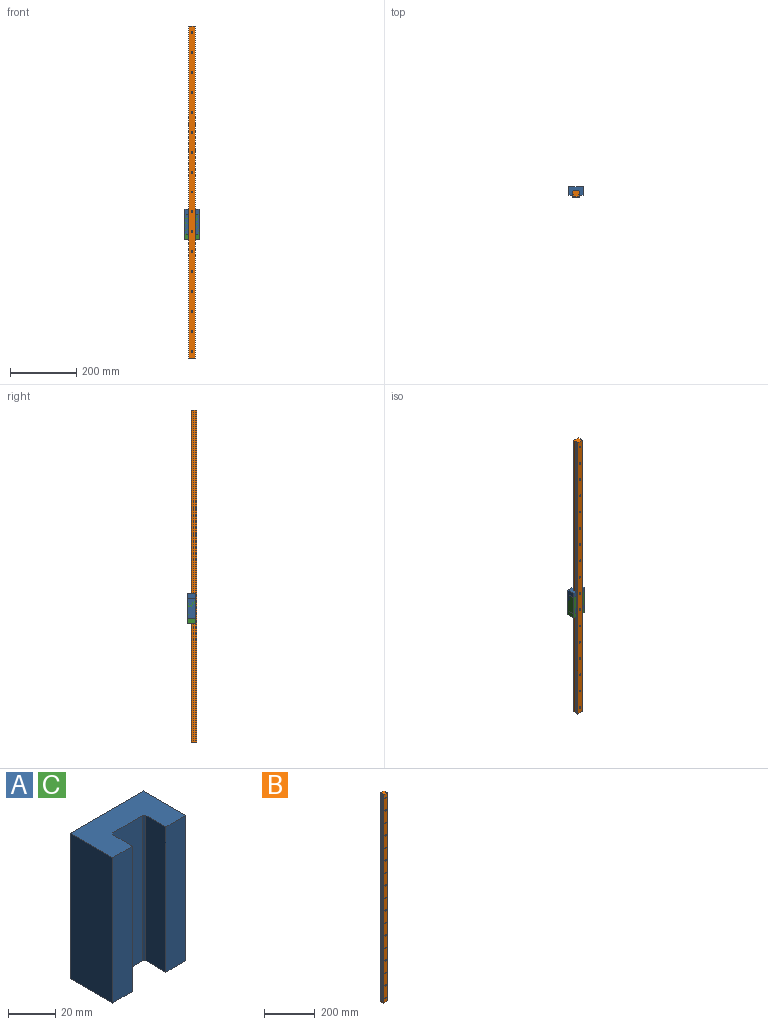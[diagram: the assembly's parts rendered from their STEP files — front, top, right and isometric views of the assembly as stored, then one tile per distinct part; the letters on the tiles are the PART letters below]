
ASSEMBLY  parts=3 mates=4
PART A: 20 faces, bbox 44x25.4x75.5 mm
  f0: plane 75.5x44mm, normal (0,1,0), area 3243.5mm2, adj f1,f9,f10,f11,f12,f14,f16,f18
  f1: plane 75.5x25.4mm, normal (-1,0,0), area 1917.7mm2, adj f0,f2,f10,f11
  f2: plane 75.5x12mm, normal (0,-1,0), area 906mm2, adj f1,f3,f10,f11
  f3: plane 75.5x11.9mm, normal (1,0,0), area 898.4mm2, adj f2,f4,f10,f11
  f4: plane 75.5x1mm, normal (0.71,-0.71,0), area 106.8mm2, adj f3,f5,f10,f11
  f5: plane 75.5x18mm, normal (0,-1,0), area 1359mm2, adj f4,f6,f10,f11
  f6: plane 75.5x1mm, normal (-0.71,-0.71,0), area 106.8mm2, adj f5,f7,f10,f11
  f7: plane 75.5x11.9mm, normal (-1,0,0), area 898.4mm2, adj f6,f8,f10,f11
  f8: plane 75.5x12mm, normal (0,-1,0), area 906mm2, adj f7,f9,f10,f11
  f9: plane 75.5x25.4mm, normal (1,0,0), area 1917.7mm2, adj f0,f8,f10,f11
  f10: plane 44x25.4mm, normal (0,0,1), area 860.6mm2, adj f0,f1,f2,f3,f4,f5,f6,f7
  f11: plane 44x25.4mm, normal (0,0,-1), area 860.6mm2, adj f0,f1,f2,f3,f4,f5,f6,f7
  f12: cylinder r=2.5mm len=5mm, axis (0,1,0), area 78.5mm2, adj f0,f13
  f13: plane 5x5mm, normal (0,1,0), area 19.6mm2, adj f12
  f14: cylinder r=2.5mm len=5mm, axis (0,1,0), area 78.5mm2, adj f0,f15
  f15: plane 5x5mm, normal (0,1,0), area 19.6mm2, adj f14
  f16: cylinder r=2.5mm len=5mm, axis (0,1,0), area 78.5mm2, adj f0,f17
  f17: plane 5x5mm, normal (0,1,0), area 19.6mm2, adj f16
  f18: cylinder r=2.5mm len=5mm, axis (0,1,0), area 78.5mm2, adj f0,f19
  f19: plane 5x5mm, normal (0,1,0), area 19.6mm2, adj f18
PART B: 65 faces, bbox 20x17.5x1000 mm
  f0: plane 1000x2.5mm, normal (0.72,-0.69,0), area 3467.8mm2, adj f1,f11,f12,f13
  f1: plane 1000x6.9mm, normal (1,0,0), area 6900mm2, adj f0,f2,f12,f13
  f2: plane 1000x1mm, normal (0.71,0.71,0), area 1414.2mm2, adj f1,f3,f12,f13
  f3: plane 1000x18mm, normal (0,1,0), area 16795mm2, adj f2,f4,f12,f13,f14,f17,f20,f23
  f4: plane 1000x1mm, normal (-0.71,0.71,0), area 1414.2mm2, adj f3,f5,f12,f13
  f5: plane 1000x6.9mm, normal (-1,0,0), area 6900mm2, adj f4,f6,f12,f13
  f6: plane 1000x2.5mm, normal (-0.72,-0.69,0), area 3467.8mm2, adj f5,f7,f12,f13
  f7: plane 1000x2.5mm, normal (-0.72,0.69,0), area 3467.8mm2, adj f6,f8,f12,f13
  f8: plane 1000x4.6mm, normal (-1,0,0), area 4600mm2, adj f7,f9,f12,f13
  f9: plane 1000x20mm, normal (0,-1,0), area 19519.3mm2, adj f8,f10,f12,f13,f16,f19,f22,f25
  f10: plane 1000x4.6mm, normal (1,0,0), area 4600mm2, adj f9,f11,f12,f13
  f11: plane 1000x2.5mm, normal (0.72,0.69,0), area 3467.8mm2, adj f0,f10,f12,f13
  f12: plane 20x17.5mm, normal (0,0,1), area 337mm2, adj f0,f1,f2,f3,f4,f5,f6,f7
  f13: plane 20x17.5mm, normal (0,0,-1), area 337mm2, adj f0,f1,f2,f3,f4,f5,f6,f7
  f14: cylinder r=4.75mm len=9.5mm, axis (0,1,0), area 253.7mm2, adj f3,f15
  f15: plane 9.5x9.5mm, normal (0,1,0), area 42.6mm2, adj f14,f16
  f16: cylinder r=3mm len=9mm, axis (0,1,0), area 169.6mm2, adj f9,f15
  f17: cylinder r=4.75mm len=9.5mm, axis (0,1,0), area 253.7mm2, adj f3,f18
  f18: plane 9.5x9.5mm, normal (0,1,0), area 42.6mm2, adj f17,f19
  f19: cylinder r=3mm len=9mm, axis (0,1,0), area 169.6mm2, adj f9,f18
  f20: cylinder r=4.75mm len=9.5mm, axis (0,1,0), area 253.7mm2, adj f3,f21
  f21: plane 9.5x9.5mm, normal (0,1,0), area 42.6mm2, adj f20,f22
  f22: cylinder r=3mm len=9mm, axis (0,1,0), area 169.6mm2, adj f9,f21
  f23: cylinder r=4.75mm len=9.5mm, axis (0,1,0), area 253.7mm2, adj f3,f24
  f24: plane 9.5x9.5mm, normal (0,1,0), area 42.6mm2, adj f23,f25
  f25: cylinder r=3mm len=9mm, axis (0,1,0), area 169.6mm2, adj f9,f24
  f26: cylinder r=4.75mm len=9.5mm, axis (0,1,0), area 253.7mm2, adj f3,f27
  f27: plane 9.5x9.5mm, normal (0,1,0), area 42.6mm2, adj f26,f28
  f28: cylinder r=3mm len=9mm, axis (0,1,0), area 169.6mm2, adj f9,f27
  f29: cylinder r=4.75mm len=9.5mm, axis (0,1,0), area 253.7mm2, adj f3,f30
  f30: plane 9.5x9.5mm, normal (0,1,0), area 42.6mm2, adj f29,f31
  f31: cylinder r=3mm len=9mm, axis (0,1,0), area 169.6mm2, adj f9,f30
  f32: cylinder r=4.75mm len=9.5mm, axis (0,1,0), area 253.7mm2, adj f3,f33
  f33: plane 9.5x9.5mm, normal (0,1,0), area 42.6mm2, adj f32,f34
  f34: cylinder r=3mm len=9mm, axis (0,1,0), area 169.6mm2, adj f9,f33
  f35: cylinder r=4.75mm len=9.5mm, axis (0,1,0), area 253.7mm2, adj f3,f36
  f36: plane 9.5x9.5mm, normal (0,1,0), area 42.6mm2, adj f35,f37
  f37: cylinder r=3mm len=9mm, axis (0,1,0), area 169.6mm2, adj f9,f36
  f38: cylinder r=4.75mm len=9.5mm, axis (0,1,0), area 253.7mm2, adj f3,f39
  f39: plane 9.5x9.5mm, normal (0,1,0), area 42.6mm2, adj f38,f40
  f40: cylinder r=3mm len=9mm, axis (0,1,0), area 169.6mm2, adj f9,f39
  f41: cylinder r=4.75mm len=9.5mm, axis (0,1,0), area 253.7mm2, adj f3,f42
  f42: plane 9.5x9.5mm, normal (0,1,0), area 42.6mm2, adj f41,f43
  f43: cylinder r=3mm len=9mm, axis (0,1,0), area 169.6mm2, adj f9,f42
  f44: cylinder r=4.75mm len=9.5mm, axis (0,1,0), area 253.7mm2, adj f3,f45
  f45: plane 9.5x9.5mm, normal (0,1,0), area 42.6mm2, adj f44,f46
  f46: cylinder r=3mm len=9mm, axis (0,1,0), area 169.6mm2, adj f9,f45
  f47: cylinder r=4.75mm len=9.5mm, axis (0,1,0), area 253.7mm2, adj f3,f48
  f48: plane 9.5x9.5mm, normal (0,1,0), area 42.6mm2, adj f47,f49
  f49: cylinder r=3mm len=9mm, axis (0,1,0), area 169.6mm2, adj f9,f48
  f50: cylinder r=4.75mm len=9.5mm, axis (0,1,0), area 253.7mm2, adj f3,f51
  f51: plane 9.5x9.5mm, normal (0,1,0), area 42.6mm2, adj f50,f52
  f52: cylinder r=3mm len=9mm, axis (0,1,0), area 169.6mm2, adj f9,f51
  f53: cylinder r=4.75mm len=9.5mm, axis (0,1,0), area 253.7mm2, adj f3,f54
  f54: plane 9.5x9.5mm, normal (0,1,0), area 42.6mm2, adj f53,f55
  f55: cylinder r=3mm len=9mm, axis (0,1,0), area 169.6mm2, adj f9,f54
  f56: cylinder r=4.75mm len=9.5mm, axis (0,1,0), area 253.7mm2, adj f3,f57
  f57: plane 9.5x9.5mm, normal (0,1,0), area 42.6mm2, adj f56,f58
  f58: cylinder r=3mm len=9mm, axis (0,1,0), area 169.6mm2, adj f9,f57
  f59: cylinder r=4.75mm len=9.5mm, axis (0,1,0), area 253.7mm2, adj f3,f60
  f60: plane 9.5x9.5mm, normal (0,1,0), area 42.6mm2, adj f59,f61
  f61: cylinder r=3mm len=9mm, axis (0,1,0), area 169.6mm2, adj f9,f60
  f62: cylinder r=4.75mm len=9.5mm, axis (0,1,0), area 253.7mm2, adj f3,f63
  f63: plane 9.5x9.5mm, normal (0,1,0), area 42.6mm2, adj f62,f64
  f64: cylinder r=3mm len=9mm, axis (0,1,0), area 169.6mm2, adj f9,f63
PART C: same geometry as A
PLACE A t=(-99.15,147.51,372.25)mm
PLACE B at identity
PLACE C t=(-99.15,147.51,356.95)mm
MATE planar C.f5 <-> B.f50  axis (0,-1,0) through (-7.08,30.61,394.7)mm
MATE planar C.f3 <-> B.f5  axis (1,0,0) through (-17.08,23.66,394.7)mm
MATE planar A.f5 <-> B.f50  axis (0,-1,0) through (-7.08,30.61,410)mm
MATE planar A.f3 <-> B.f5  axis (1,0,0) through (-17.08,23.66,410)mm
